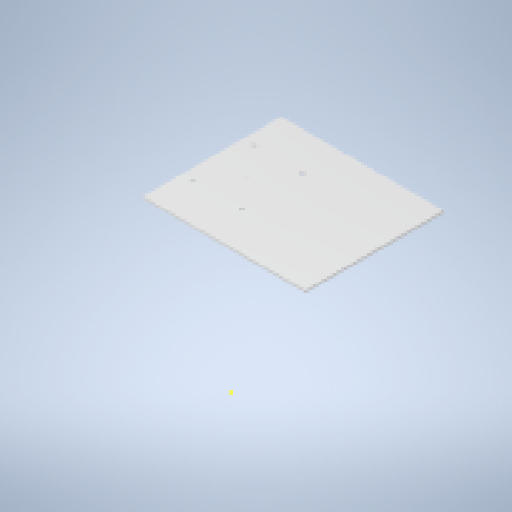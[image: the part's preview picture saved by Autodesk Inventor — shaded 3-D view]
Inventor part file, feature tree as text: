
AUTODESK INVENTOR PART (.ipt)
format: ipt  version: 2023.2 (Build 272271000, 271)  size: 192,000 bytes
history: native  units: in
note: dims shown in document units (in); Inventor stores cm internally (conversion verified against a paired STEP export)
features: extrude x3, sketch x2
ambient origin geometry x8: Origin, YZ Plane, XZ Plane, XY Plane, X Axis, Y Axis, Z Axis, Center Point
bodies: Solid1 (feature_tree)
feature tree (5):
  sketch  "Sketch1"  dims[d2=0.5394in d4=2.3819in]
  extrude  "Extrusion1"  Depth=2.3819in
  sketch  "Sketch2"  dims[d5=0.2008in d6=0.2008in d7=0.2008in d8=0.2795in d9=0.1181in d10=0.0in d11=0.0787in d12=0.1181in d13=0.0in d15=1.9685in d17=1.9685in d18=0.9843in d19=0.6004in d20=0.2008in d21=0.5118in d22=0.9843in d23=6.2992in d24=2.9528in d25=0.0in d26=0.0in]
  extrude  "Extrusion2"  Depth=6.2992in
  extrude  "Extrusion3"  Depth=6.2992in
